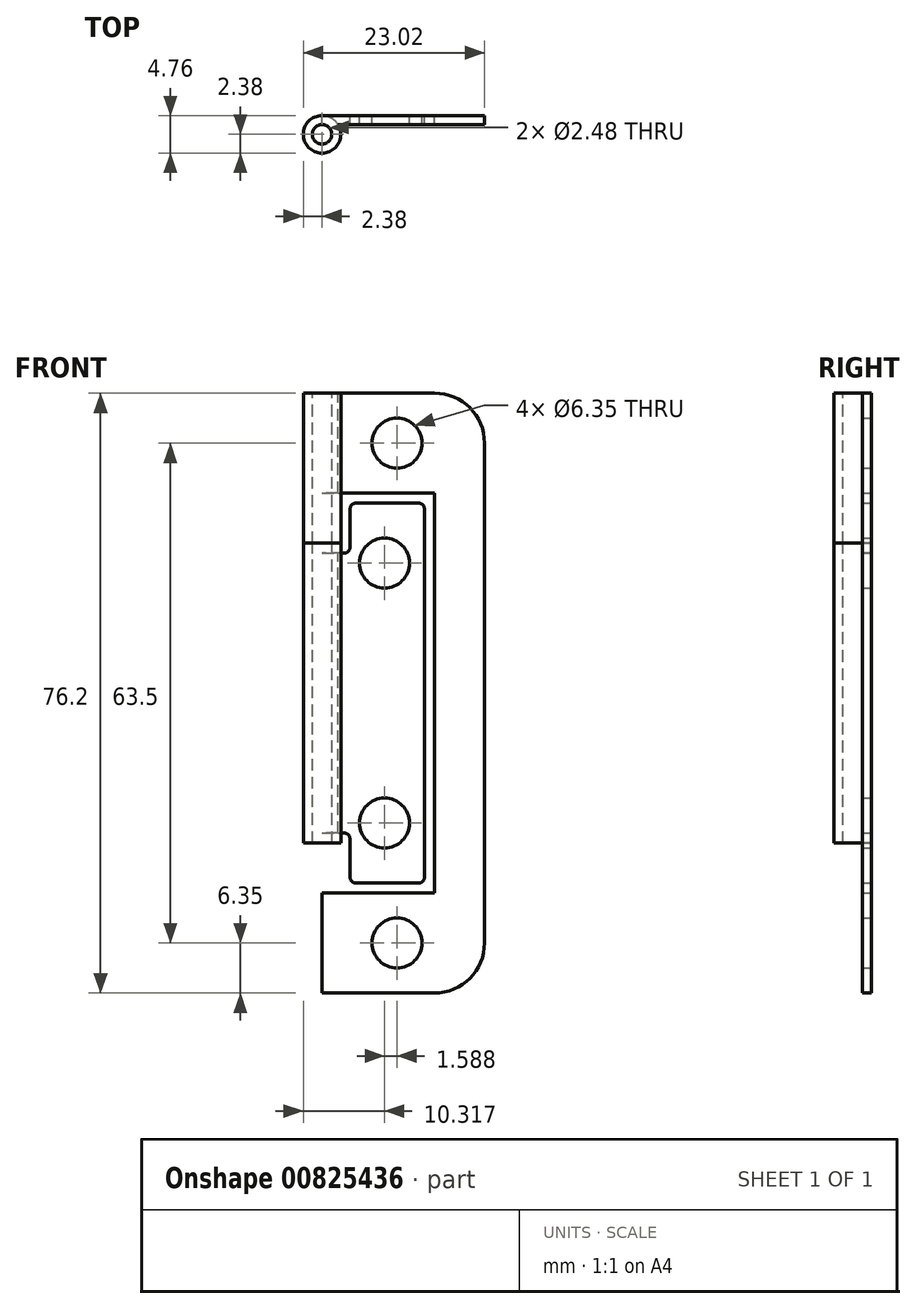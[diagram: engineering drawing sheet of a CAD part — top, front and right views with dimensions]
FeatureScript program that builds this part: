
annotation { "Feature Type Name" : "Feature", "Feature Type Description" : "" }
export const myFeature = defineFeature(function(context is Context, id is Id, definition is map)
    precondition{}
    {
        {
            assignVariable(context, id + "F0", {"name" : "hinge_height", "anyValue" : 76.2 * mm});
        }
        {
            var Q0;
            Q0=qCreatedBy(makeId("Front.planeOp"),FACE);
            var sketch = newSketch(context, id + "F1", { "sketchPlane" : qUnion([Q0])});
            skLineSegment(sketch, "E0.bottom", {"start": v(0, 0) * mm, "end": v(14.29, 0) * mm});
            skLineSegment(sketch, "E0.top", {"start": v(0, 76.2) * mm, "end": v(14.29, 76.2) * mm});
            skLineSegment(sketch, "E0.left", {"start": v(0, 0) * mm, "end": v(0, 12.7) * mm});
            skLineSegment(sketch, "E0.right", {"start": v(20.64, 6.35) * mm, "end": v(20.64, 69.85) * mm});
            skPoint(sketch, "E1.visualSharp", {"position": v(20.64, 76.2) * mm});
            skArc(sketch, "E1.filletArc", {"start": v(20.64, 69.85) * mm, "mid": v(18.78, 74.34) * mm, "end": v(14.29, 76.2) * mm});
            skPoint(sketch, "E2.visualSharp", {"position": v(20.64, 0) * mm});
            skArc(sketch, "E2.filletArc", {"start": v(14.29, 0) * mm, "mid": v(18.78, 1.86) * mm, "end": v(20.64, 6.35) * mm});
            skLineSegment(sketch, "E3.bottom", {"start": v(0, 63.5) * mm, "end": v(14.29, 63.5) * mm});
            skLineSegment(sketch, "E3.top", {"start": v(0, 12.7) * mm, "end": v(14.29, 12.7) * mm});
            skLineSegment(sketch, "E3.right", {"start": v(14.29, 63.5) * mm, "end": v(14.29, 12.7) * mm});
            skLineSegment(sketch, "E4.trimOffspring", {"start": v(0, 63.5) * mm, "end": v(0, 76.2) * mm});
            skCircle(sketch, "E5", {"center": v(9.53, 69.85) * mm, "radius": 3.18 * mm});
            skLineSegment(sketch, "E6", {"start": v(9.53, 76.2) * mm, "end": v(9.53, 63.5) * mm, "construction": true});
            skCircle(sketch, "E7.MirrorC", {"center": v(9.53, 6.35) * mm, "radius": 3.18 * mm});
            skLineSegment(sketch, "E8", {"start": v(9.53, 6.35) * mm, "end": v(9.53, 12.7) * mm, "construction": true});
            skLineSegment(sketch, "E9", {"start": v(9.53, 6.35) * mm, "end": v(9.53, 0) * mm, "construction": true});
            skSolve(sketch);
        }
        {
            var Q0;
            Q0=qSketchRegion(id+"F1",true);
            extrude(context, id + "F2", {"entities" : qUnion([Q0]), "endBound" : BoundingType.SYMMETRIC, "depth" : 1.14 * mm, "offsetDistance" : 25.4 * mm});
        }
        {
            var Q0;
            Q0=makeQuery(id+"F2.opExtrude","SWEPT_FACE",FACE,{"disambiguationData":[OSD([sQuery(id+"F1.wireOp",EDGE,"E0.top")])]});
            var sketch = newSketch(context, id + "F3", { "sketchPlane" : qUnion([Q0])});
            skCircle(sketch, "E10", {"center": v(0, -1.8) * mm, "radius": 2.38 * mm});
            skCircle(sketch, "E11", {"center": v(0, -1.8) * mm, "radius": 1.24 * mm});
            skSolve(sketch);
        }
        {
            var Q0;
            Q0=qSketchRegion(id+"F3",true);
            extrude(context, id + "F4", {"entities" : qUnion([Q0]), "operationType" : NewBodyOperationType.ADD, "oppositeDirection" : true, "depth" : 19.05 * mm, "offsetDistance" : 25.4 * mm});
        }
        {
            var Q0;
            Q0=qCreatedBy(makeId("Top.planeOp"),FACE);
            cPlane(context, id + "F5", {"entities" : qUnion([Q0]), "cplaneType" : CPlaneType.OFFSET, "offset" : getVariable(context, 'hinge_height') / 2, "width" : 152.4 * mm, "height" : 152.4 * mm});
        }
        {
            var Q0;
            Q0=makeQuery(id+"F4.opExtrude","CAP_FACE",FACE,{"disambiguationData":[OSD([sQuery(id+"F3.wireOp",EDGE,"E10"),sQuery(id+"F3.wireOp",EDGE,"E11")])],"isStart":false});
            var sketch = newSketch(context, id + "F6", { "sketchPlane" : qUnion([Q0])});
            skCircle(sketch, "E12.0", {"center": v(0, 1.8) * mm, "radius": 1.24 * mm});
            skCircle(sketch, "E13.0", {"center": v(0, 1.8) * mm, "radius": 2.38 * mm});
            skSolve(sketch);
        }
        {
            var Q0;
            Q0=qSketchRegion(id+"F6",true);
            extrude(context, id + "F7", {"entities" : qUnion([Q0]), "depth" : 38.1 * mm, "offsetDistance" : 25.4 * mm});
        }
        {
            var Q0;
            Q0=qCreatedBy(makeId("Front.planeOp"),FACE);
            var sketch = newSketch(context, id + "F8", { "sketchPlane" : qUnion([Q0])});
            skLineSegment(sketch, "E14.bottom", {"start": v(4.32, 62.23) * mm, "end": v(12.26, 62.23) * mm});
            skLineSegment(sketch, "E14.top", {"start": v(4.32, 13.97) * mm, "end": v(12.26, 13.97) * mm});
            skLineSegment(sketch, "E14.left", {"start": v(3.56, 61.47) * mm, "end": v(3.56, 56.64) * mm});
            skLineSegment(sketch, "E14.right", {"start": v(13.02, 61.47) * mm, "end": v(13.02, 14.73) * mm});
            skLineSegment(sketch, "E15", {"start": v(2.8, 55.88) * mm, "end": v(0, 55.88) * mm});
            skLineSegment(sketch, "E16", {"start": v(0, 55.88) * mm, "end": v(0, 20.32) * mm});
            skLineSegment(sketch, "E17", {"start": v(0, 20.32) * mm, "end": v(2.8, 20.32) * mm});
            skLineSegment(sketch, "E18.trimOffspring", {"start": v(3.56, 19.56) * mm, "end": v(3.56, 14.73) * mm});
            skPoint(sketch, "E19.visualSharp", {"position": v(3.56, 55.88) * mm});
            skArc(sketch, "E19.filletArc", {"start": v(2.8, 55.88) * mm, "mid": v(3.33, 56.1) * mm, "end": v(3.56, 56.64) * mm});
            skPoint(sketch, "E20.visualSharp", {"position": v(3.56, 20.32) * mm});
            skArc(sketch, "E20.filletArc", {"start": v(3.56, 19.56) * mm, "mid": v(3.33, 20.1) * mm, "end": v(2.8, 20.32) * mm});
            skCircle(sketch, "E21", {"center": v(7.94, 54.61) * mm, "radius": 3.18 * mm});
            skCircle(sketch, "E22", {"center": v(7.94, 21.6) * mm, "radius": 3.18 * mm});
            skPoint(sketch, "E23.visualSharp", {"position": v(13.02, 62.23) * mm});
            skArc(sketch, "E23.filletArc", {"start": v(13.02, 61.47) * mm, "mid": v(12.8, 62) * mm, "end": v(12.26, 62.23) * mm});
            skPoint(sketch, "E24.visualSharp", {"position": v(13.02, 13.97) * mm});
            skArc(sketch, "E24.filletArc", {"start": v(12.26, 13.97) * mm, "mid": v(12.8, 14.2) * mm, "end": v(13.02, 14.73) * mm});
            skPoint(sketch, "E25.visualSharp", {"position": v(3.56, 13.97) * mm});
            skArc(sketch, "E25.filletArc", {"start": v(3.56, 14.73) * mm, "mid": v(3.78, 14.2) * mm, "end": v(4.32, 13.97) * mm});
            skPoint(sketch, "E26.visualSharp", {"position": v(3.56, 62.23) * mm});
            skArc(sketch, "E26.filletArc", {"start": v(4.32, 62.23) * mm, "mid": v(3.78, 62) * mm, "end": v(3.56, 61.47) * mm});
            skLineSegment(sketch, "E27", {"start": v(7.94, 62.23) * mm, "end": v(7.94, 54.61) * mm, "construction": true});
            skLineSegment(sketch, "E28", {"start": v(7.94, 21.6) * mm, "end": v(7.94, 13.97) * mm, "construction": true});
            skSolve(sketch);
        }
        {
            var Q0;
            Q0=qSketchRegion(id+"F8",true);
            extrude(context, id + "F9", {"entities" : qUnion([Q0]), "operationType" : NewBodyOperationType.ADD, "endBound" : BoundingType.SYMMETRIC, "depth" : 1.14 * mm, "offsetDistance" : 25.4 * mm});
        }
    });
